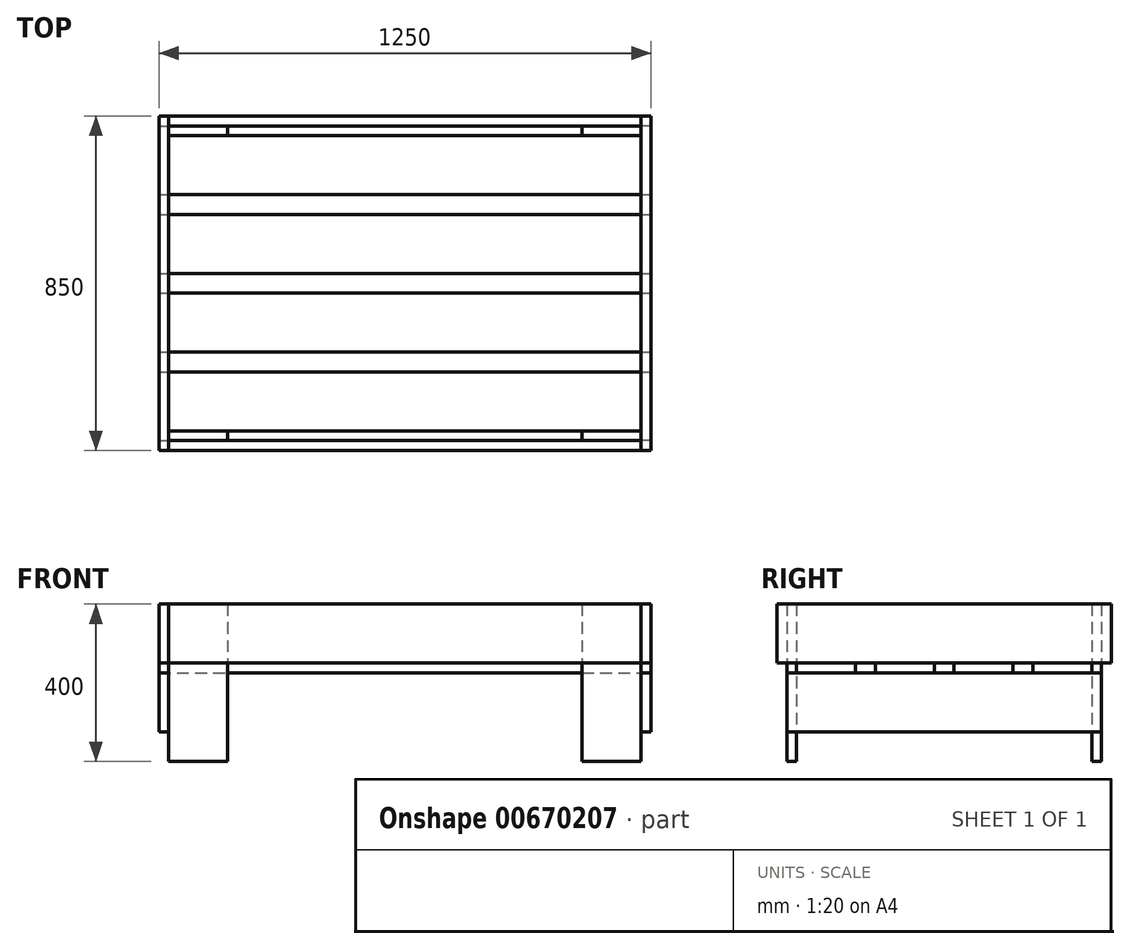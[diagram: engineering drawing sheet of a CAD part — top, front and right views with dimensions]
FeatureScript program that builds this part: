
annotation { "Feature Type Name" : "Feature", "Feature Type Description" : "" }
export const myFeature = defineFeature(function(context is Context, id is Id, definition is map)
    precondition{}
    {
        {
            var Q0;
            Q0=qCreatedBy(makeId("Top.planeOp"),FACE);
            var sketch = newSketch(context, id + "F0", { "sketchPlane" : qUnion([Q0])});
            skLineSegment(sketch, "E0", {"start": v(588.73, 398.16) * mm, "end": v(-611.27, 398.16) * mm, "construction": true});
            skLineSegment(sketch, "E1", {"start": v(-611.27, 398.16) * mm, "end": v(-611.27, -401.84) * mm, "construction": true});
            skLineSegment(sketch, "E2", {"start": v(-611.27, -401.84) * mm, "end": v(588.73, -401.84) * mm, "construction": true});
            skLineSegment(sketch, "E3.bottom", {"start": v(-611.27, 398.16) * mm, "end": v(588.73, 398.16) * mm});
            skLineSegment(sketch, "E3.top", {"start": v(-611.27, 423.16) * mm, "end": v(588.73, 423.16) * mm});
            skLineSegment(sketch, "E3.left", {"start": v(-611.27, 398.16) * mm, "end": v(-611.27, 423.16) * mm});
            skLineSegment(sketch, "E3.right", {"start": v(588.73, 398.16) * mm, "end": v(588.73, 423.16) * mm});
            skLineSegment(sketch, "E4.bottom", {"start": v(-611.27, -401.84) * mm, "end": v(588.73, -401.84) * mm});
            skLineSegment(sketch, "E4.top", {"start": v(-611.27, -426.84) * mm, "end": v(588.73, -426.84) * mm});
            skLineSegment(sketch, "E4.left", {"start": v(-611.27, -401.84) * mm, "end": v(-611.27, -426.84) * mm});
            skLineSegment(sketch, "E4.right", {"start": v(588.73, -401.84) * mm, "end": v(588.73, -426.84) * mm});
            skLineSegment(sketch, "E5.bottom", {"start": v(-611.27, -426.84) * mm, "end": v(-636.27, -426.84) * mm});
            skLineSegment(sketch, "E5.top", {"start": v(-611.27, 423.16) * mm, "end": v(-636.27, 423.16) * mm});
            skLineSegment(sketch, "E5.left", {"start": v(-611.27, -426.84) * mm, "end": v(-611.27, 423.16) * mm});
            skLineSegment(sketch, "E5.right", {"start": v(-636.27, -426.84) * mm, "end": v(-636.27, 423.16) * mm});
            skLineSegment(sketch, "E6.bottom", {"start": v(588.73, -426.84) * mm, "end": v(613.73, -426.84) * mm});
            skLineSegment(sketch, "E6.top", {"start": v(588.73, 423.16) * mm, "end": v(613.73, 423.16) * mm});
            skLineSegment(sketch, "E6.left", {"start": v(588.73, -426.84) * mm, "end": v(588.73, 423.16) * mm});
            skLineSegment(sketch, "E6.right", {"start": v(613.73, -426.84) * mm, "end": v(613.73, 423.16) * mm});
            skSolve(sketch);
        }
        {
            var Q0;
            {var subQ3=sQuery(id+"F0.wireOp",EDGE,"E5.bottom");Q0=makeQuery(id+"F0.imprint","IMPRINT",FACE,{"disambiguationData":[TD([[makeQuery(id+"F0.imprint","IMPRINT",EDGE,{"derivedFrom":subQ3}),-1.0]])]});}
            var Q1;
            {var subQ3=sQuery(id+"F0.wireOp",EDGE,"E6.bottom");Q1=makeQuery(id+"F0.imprint","IMPRINT",FACE,{"disambiguationData":[TD([[makeQuery(id+"F0.imprint","IMPRINT",EDGE,{"derivedFrom":subQ3}),1.0]])]});}
            extrude(context, id + "F1", {"entities" : qUnion([Q0, Q1]), "depth" : 150 * mm, "offsetDistance" : 25 * mm, "symmetric" : true});
        }
        {
            var Q0;
            {var subQ0=sQuery(id+"F0.wireOp",EDGE,"E3.bottom");Q0=makeQuery(id+"F0.imprint","IMPRINT",FACE,{"disambiguationData":[TD([[makeQuery(id+"F0.imprint","IMPRINT",EDGE,{"derivedFrom":subQ0}),1.0]])]});}
            var Q1;
            {var subQ0=sQuery(id+"F0.wireOp",EDGE,"E4.bottom");Q1=makeQuery(id+"F0.imprint","IMPRINT",FACE,{"disambiguationData":[TD([[makeQuery(id+"F0.imprint","IMPRINT",EDGE,{"derivedFrom":subQ0}),-1.0]])]});}
            extrude(context, id + "F2", {"entities" : qUnion([Q0, Q1]), "depth" : 150 * mm, "offsetDistance" : 25 * mm, "symmetric" : true});
        }
        {
            var Q0;
            Q0=makeQuery(id+"F2.opExtrude","SWEPT_FACE",FACE,{"disambiguationData":[OSD([sQuery(id+"F0.wireOp",EDGE,"E3.bottom")])]});
            var sketch = newSketch(context, id + "F3", { "sketchPlane" : qUnion([Q0])});
            skLineSegment(sketch, "E7.bottom", {"start": v(-611.27, 75) * mm, "end": v(-461.27, 75) * mm});
            skLineSegment(sketch, "E7.top", {"start": v(-611.27, -325) * mm, "end": v(-461.27, -325) * mm});
            skLineSegment(sketch, "E7.left", {"start": v(-611.27, 75) * mm, "end": v(-611.27, -325) * mm});
            skLineSegment(sketch, "E7.right", {"start": v(-461.27, 75) * mm, "end": v(-461.27, -325) * mm});
            skLineSegment(sketch, "E8.bottom", {"start": v(588.73, 75) * mm, "end": v(438.73, 75) * mm});
            skLineSegment(sketch, "E8.top", {"start": v(588.73, -325) * mm, "end": v(438.73, -325) * mm});
            skLineSegment(sketch, "E8.left", {"start": v(588.73, 75) * mm, "end": v(588.73, -325) * mm});
            skLineSegment(sketch, "E8.right", {"start": v(438.73, 75) * mm, "end": v(438.73, -325) * mm});
            skSolve(sketch);
        }
        {
            var Q0;
            {var subQ0=sQuery(id+"F3.wireOp",EDGE,"E8.top");Q0=makeQuery(id+"F3.imprint","IMPRINT",FACE,{"disambiguationData":[TD([[makeQuery(id+"F3.imprint","IMPRINT",EDGE,{"derivedFrom":subQ0}),-1.0]])]});}
            var Q1;
            {var subQ0=sQuery(id+"F3.wireOp",EDGE,"E8.bottom");Q1=makeQuery(id+"F3.imprint","IMPRINT",FACE,{"disambiguationData":[TD([[makeQuery(id+"F3.imprint","IMPRINT",EDGE,{"derivedFrom":subQ0}),-1.0]])]});}
            var Q2;
            {var subQ0=sQuery(id+"F3.wireOp",EDGE,"E7.bottom");Q2=makeQuery(id+"F3.imprint","IMPRINT",FACE,{"disambiguationData":[TD([[makeQuery(id+"F3.imprint","IMPRINT",EDGE,{"derivedFrom":subQ0}),-1.0]])]});}
            var Q3;
            {var subQ0=sQuery(id+"F3.wireOp",EDGE,"E7.top");Q3=makeQuery(id+"F3.imprint","IMPRINT",FACE,{"disambiguationData":[TD([[makeQuery(id+"F3.imprint","IMPRINT",EDGE,{"derivedFrom":subQ0}),1.0]])]});}
            extrude(context, id + "F4", {"entities" : qUnion([Q0, Q1, Q2, Q3]), "depth" : 25 * mm, "offsetDistance" : 25 * mm});
        }
        {
            var Q0;
            Q0=makeQuery(id+"F4.opExtrude","CAP_FACE",FACE,{"disambiguationData":[OSD([sQuery(id+"F3.wireOp",EDGE,"E7.bottom"),sQuery(id+"F3.wireOp",EDGE,"E7.top"),sQuery(id+"F3.wireOp",EDGE,"E7.left"),sQuery(id+"F3.wireOp",EDGE,"E7.right")])],"isStart":false});
            var Q1;
            Q1=makeQuery(id+"F4.opExtrude","CAP_FACE",FACE,{"disambiguationData":[OSD([sQuery(id+"F3.wireOp",EDGE,"E8.bottom"),sQuery(id+"F3.wireOp",EDGE,"E8.top"),sQuery(id+"F3.wireOp",EDGE,"E8.left"),sQuery(id+"F3.wireOp",EDGE,"E8.right")])],"isStart":false});
            extrude(context, id + "F5", {"entities" : qUnion([Q0, Q1]), "depth" : 775 * mm, "offsetDistance" : 25 * mm, "hasSecondDirection" : true, "secondDirectionOppositeDirection" : false, "secondDirectionDepth" : 750 * mm});
        }
        {
            var Q0;
            Q0=makeQuery(id+"F1.opExtrude","CAP_FACE",FACE,{"disambiguationData":[OSD([sQuery(id+"F0.wireOp",EDGE,"E5.bottom"),sQuery(id+"F0.wireOp",EDGE,"E5.top"),sQuery(id+"F0.wireOp",EDGE,"E5.left"),sQuery(id+"F0.wireOp",EDGE,"E5.right")])],"isStart":true});
            var sketch = newSketch(context, id + "F6", { "sketchPlane" : qUnion([Q0])});
            skLineSegment(sketch, "E9", {"start": v(-636.27, 426.84) * mm, "end": v(-665.87, 426.84) * mm, "construction": true});
            skLineSegment(sketch, "E10", {"start": v(-481.05, 376.84) * mm, "end": v(-707.58, 376.84) * mm, "construction": true});
            skLineSegment(sketch, "E11.bottom", {"start": v(-636.27, 376.84) * mm, "end": v(613.73, 376.84) * mm});
            skLineSegment(sketch, "E11.top", {"start": v(-636.27, 226.84) * mm, "end": v(613.73, 226.84) * mm});
            skLineSegment(sketch, "E11.left", {"start": v(-636.27, 376.84) * mm, "end": v(-636.27, 226.84) * mm});
            skLineSegment(sketch, "E11.right", {"start": v(613.73, 376.84) * mm, "end": v(613.73, 226.84) * mm});
            skLineSegment(sketch, "E12", {"start": v(-636.27, -423.16) * mm, "end": v(-766.82, -423.16) * mm, "construction": true});
            skLineSegment(sketch, "E13", {"start": v(-598.63, -373.16) * mm, "end": v(-752.14, -373.16) * mm, "construction": true});
            skLineSegment(sketch, "E14.bottom", {"start": v(-636.27, -373.16) * mm, "end": v(613.73, -373.16) * mm});
            skLineSegment(sketch, "E14.top", {"start": v(-636.27, -223.16) * mm, "end": v(613.73, -223.16) * mm});
            skLineSegment(sketch, "E14.left", {"start": v(-636.27, -373.16) * mm, "end": v(-636.27, -223.16) * mm});
            skLineSegment(sketch, "E14.right", {"start": v(613.73, -373.16) * mm, "end": v(613.73, -223.16) * mm});
            skLineSegment(sketch, "E15", {"start": v(-874.38, -173.16) * mm, "end": v(-449.4, -173.16) * mm, "construction": true});
            skLineSegment(sketch, "E16", {"start": v(-532.32, 176.84) * mm, "end": v(-767.27, 176.84) * mm, "construction": true});
            skLineSegment(sketch, "E17.bottom", {"start": v(-636.27, -173.16) * mm, "end": v(613.73, -173.16) * mm});
            skLineSegment(sketch, "E17.top", {"start": v(-636.27, -23.16) * mm, "end": v(613.73, -23.16) * mm});
            skLineSegment(sketch, "E17.left", {"start": v(-636.27, -173.16) * mm, "end": v(-636.27, -23.16) * mm});
            skLineSegment(sketch, "E17.right", {"start": v(613.73, -173.16) * mm, "end": v(613.73, -23.16) * mm});
            skLineSegment(sketch, "E18.bottom", {"start": v(-636.27, 176.84) * mm, "end": v(613.73, 176.84) * mm});
            skLineSegment(sketch, "E18.top", {"start": v(-636.27, 26.84) * mm, "end": v(613.73, 26.84) * mm});
            skLineSegment(sketch, "E18.left", {"start": v(-636.27, 176.84) * mm, "end": v(-636.27, 26.84) * mm});
            skLineSegment(sketch, "E18.right", {"start": v(613.73, 176.84) * mm, "end": v(613.73, 26.84) * mm});
            skSolve(sketch);
        }
        {
            var Q0;
            {var subQ0=sQuery(id+"F6.wireOp",EDGE,"E14.right");Q0=makeQuery(id+"F6.imprint","IMPRINT",FACE,{"disambiguationData":[TD([[makeQuery(id+"F6.imprint","IMPRINT",EDGE,{"derivedFrom":subQ0}),1.0]])]});}
            var Q1;
            {var subQ0=sQuery(id+"F6.wireOp",EDGE,"E14.left");Q1=makeQuery(id+"F6.imprint","IMPRINT",FACE,{"disambiguationData":[TD([[makeQuery(id+"F6.imprint","IMPRINT",EDGE,{"derivedFrom":subQ0}),1.0]])]});}
            var Q2;
            {var subQ0=sQuery(id+"F6.wireOp",EDGE,"YPR1lEAh-4hcA-x1tA-bkLg-h0Wxmnlg6Uwb.left");Q2=makeQuery(id+"F6.imprint","IMPRINT",FACE,{"disambiguationData":[TD([[makeQuery(id+"F6.imprint","IMPRINT",EDGE,{"derivedFrom":subQ0}),1.0]])]});}
            var Q3;
            {var subQ0=sQuery(id+"F6.wireOp",EDGE,"E11.left");Q3=makeQuery(id+"F6.imprint","IMPRINT",FACE,{"disambiguationData":[TD([[makeQuery(id+"F6.imprint","IMPRINT",EDGE,{"derivedFrom":subQ0}),1.0]])]});}
            var Q4;
            {var subQ0=sQuery(id+"F6.wireOp",EDGE,"E11.right");Q4=makeQuery(id+"F6.imprint","IMPRINT",FACE,{"disambiguationData":[TD([[makeQuery(id+"F6.imprint","IMPRINT",EDGE,{"derivedFrom":subQ0}),-1.0]])]});}
            var Q5;
            {var subQ0=sQuery(id+"F6.wireOp",EDGE,"YPR1lEAh-4hcA-x1tA-bkLg-h0Wxmnlg6Uwb.right");Q5=makeQuery(id+"F6.imprint","IMPRINT",FACE,{"disambiguationData":[TD([[makeQuery(id+"F6.imprint","IMPRINT",EDGE,{"derivedFrom":subQ0}),1.0]])]});}
            extrude(context, id + "F7", {"entities" : qUnion([Q0, Q1, Q2, Q3, Q4, Q5]), "depth" : 25 * mm, "offsetDistance" : 25 * mm});
        }
        {
            var Q0;
            Q0=makeQuery(id+"F4.opExtrude","SWEPT_FACE",FACE,{"disambiguationData":[OSD([sQuery(id+"F3.wireOp",EDGE,"E7.left")])]});
            var sketch = newSketch(context, id + "F8", { "sketchPlane" : qUnion([Q0])});
            skLineSegment(sketch, "E19", {"start": v(-398.16, 75) * mm, "end": v(-462.77, 75) * mm, "construction": true});
            skLineSegment(sketch, "E20", {"start": v(-363.53, -100) * mm, "end": v(-473.42, -100) * mm, "construction": true});
            skLineSegment(sketch, "E21.bottom", {"start": v(-398.16, -100) * mm, "end": v(401.84, -100) * mm});
            skLineSegment(sketch, "E21.top", {"start": v(-398.16, -250) * mm, "end": v(401.84, -250) * mm});
            skLineSegment(sketch, "E21.left", {"start": v(-398.16, -100) * mm, "end": v(-398.16, -250) * mm});
            skLineSegment(sketch, "E21.right", {"start": v(401.84, -100) * mm, "end": v(401.84, -250) * mm});
            skSolve(sketch);
        }
        {
            var Q0;
            {var subQ0=sQuery(id+"F8.wireOp",EDGE,"E21.left");Q0=makeQuery(id+"F8.imprint","IMPRINT",FACE,{"disambiguationData":[TD([[makeQuery(id+"F8.imprint","IMPRINT",EDGE,{"derivedFrom":subQ0}),1.0]])]});}
            var Q1;
            {var subQ0=sQuery(id+"F8.wireOp",EDGE,"E21.right");Q1=makeQuery(id+"F8.imprint","IMPRINT",FACE,{"disambiguationData":[TD([[makeQuery(id+"F8.imprint","IMPRINT",EDGE,{"derivedFrom":subQ0}),-1.0]])]});}
            extrude(context, id + "F9", {"entities" : qUnion([Q0, Q1]), "depth" : 25 * mm, "offsetDistance" : 25 * mm});
        }
        {
            var Q0;
            {var subQ0=sQuery(id+"F8.wireOp",EDGE,"E21.right");Q0=makeQuery(id+"F8.imprint","IMPRINT",FACE,{"disambiguationData":[TD([[makeQuery(id+"F8.imprint","IMPRINT",EDGE,{"derivedFrom":subQ0}),-1.0]])]});}
            var Q1;
            {var subQ0=sQuery(id+"F8.wireOp",EDGE,"E21.left");Q1=makeQuery(id+"F8.imprint","IMPRINT",FACE,{"disambiguationData":[TD([[makeQuery(id+"F8.imprint","IMPRINT",EDGE,{"derivedFrom":subQ0}),1.0]])]});}
            extrude(context, id + "F10", {"entities" : qUnion([Q0, Q1]), "oppositeDirection" : true, "depth" : 1225 * mm, "offsetDistance" : 25 * mm, "hasSecondDirection" : true, "secondDirectionOppositeDirection" : true, "secondDirectionDepth" : 1200 * mm});
        }
        {
            var Q0;
            {var subQ0=sQuery(id+"F6.wireOp",EDGE,"E18.right");Q0=makeQuery(id+"F6.imprint","IMPRINT",FACE,{"disambiguationData":[TD([[makeQuery(id+"F6.imprint","IMPRINT",EDGE,{"derivedFrom":subQ0}),-1.0]])]});}
            var Q1;
            {var subQ0=sQuery(id+"F6.wireOp",EDGE,"E18.left");Q1=makeQuery(id+"F6.imprint","IMPRINT",FACE,{"disambiguationData":[TD([[makeQuery(id+"F6.imprint","IMPRINT",EDGE,{"derivedFrom":subQ0}),1.0]])]});}
            var Q2;
            {var subQ0=sQuery(id+"F6.wireOp",EDGE,"E17.left");Q2=makeQuery(id+"F6.imprint","IMPRINT",FACE,{"disambiguationData":[TD([[makeQuery(id+"F6.imprint","IMPRINT",EDGE,{"derivedFrom":subQ0}),1.0]])]});}
            var Q3;
            {var subQ0=sQuery(id+"F6.wireOp",EDGE,"E17.right");Q3=makeQuery(id+"F6.imprint","IMPRINT",FACE,{"disambiguationData":[TD([[makeQuery(id+"F6.imprint","IMPRINT",EDGE,{"derivedFrom":subQ0}),1.0]])]});}
            extrude(context, id + "F11", {"entities" : qUnion([Q0, Q1, Q2, Q3]), "depth" : 25 * mm, "offsetDistance" : 25 * mm});
        }
    });
